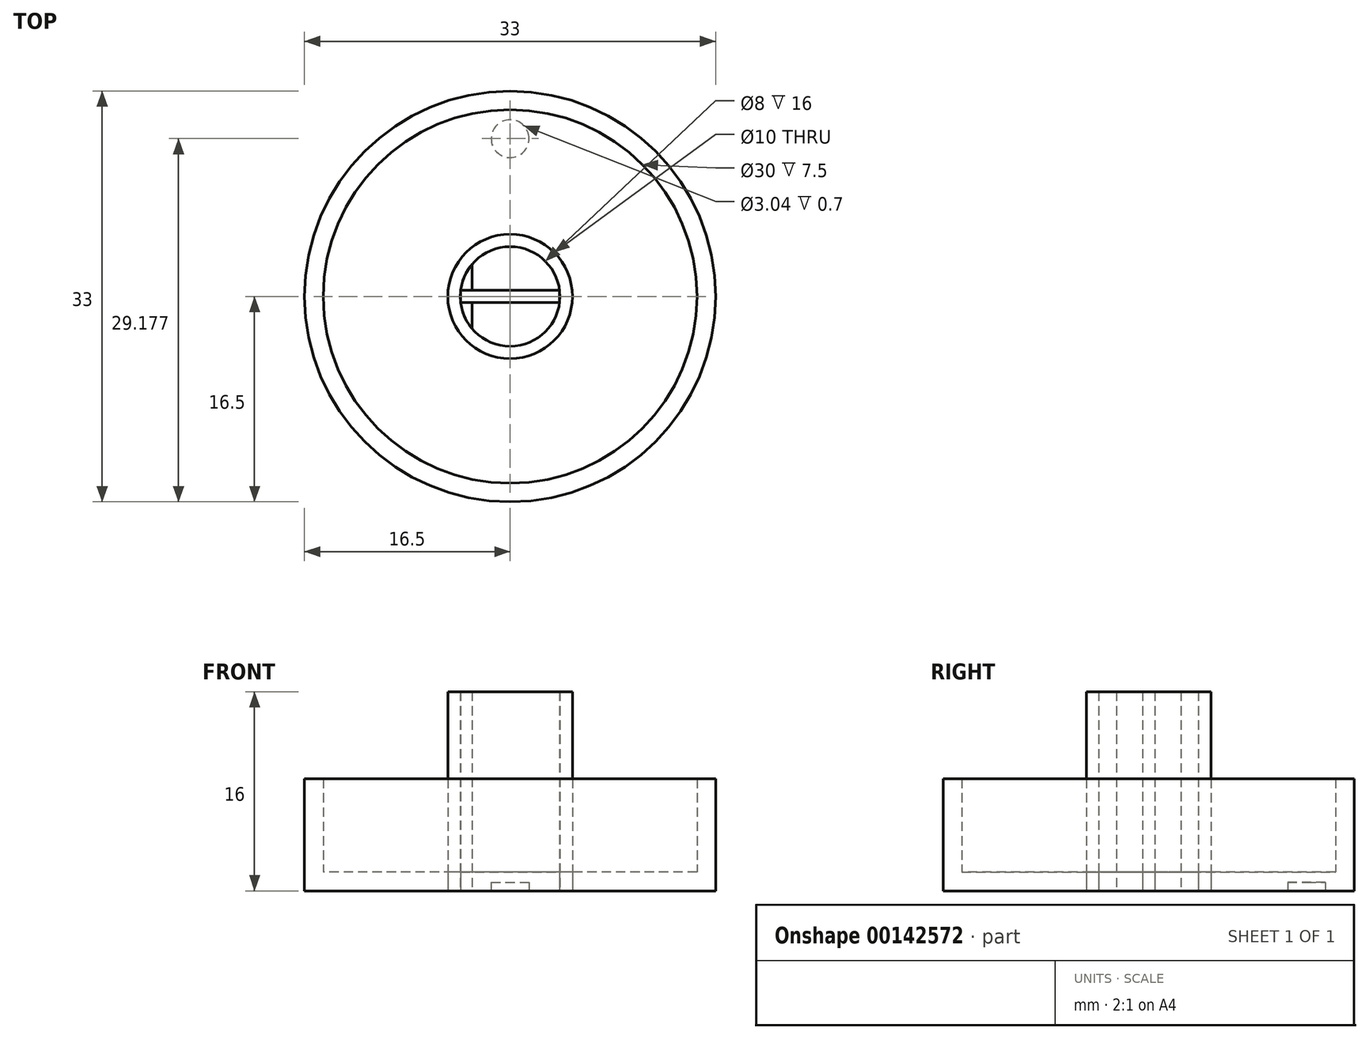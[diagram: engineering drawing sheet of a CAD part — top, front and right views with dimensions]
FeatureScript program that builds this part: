
annotation { "Feature Type Name" : "Feature", "Feature Type Description" : "" }
export const myFeature = defineFeature(function(context is Context, id is Id, definition is map)
    precondition{}
    {
        {
            var Q0;
            Q0=qCreatedBy(makeId("Top.planeOp"),FACE);
            var sketch = newSketch(context, id + "F0", { "sketchPlane" : qUnion([Q0])});
            skCircle(sketch, "E0", {"center": v(0, 0) * mm, "radius": 16.5 * mm});
            skCircle(sketch, "E1", {"center": v(0, 0) * mm, "radius": 15 * mm});
            skCircle(sketch, "E2", {"center": v(0, 0) * mm, "radius": 5 * mm});
            skCircle(sketch, "E3", {"center": v(0, 0) * mm, "radius": 4 * mm});
            skLineSegment(sketch, "E4.rect.bottom", {"start": v(-3.97, 0.5) * mm, "end": v(3.97, 0.5) * mm});
            skLineSegment(sketch, "E4.rect.top", {"start": v(-3.97, -0.5) * mm, "end": v(3.97, -0.5) * mm});
            skLineSegment(sketch, "E4.rect.left", {"start": v(-3.97, 0.5) * mm, "end": v(-3.97, -0.5) * mm});
            skLineSegment(sketch, "E4.rect.right", {"start": v(3.97, 0.5) * mm, "end": v(3.97, -0.5) * mm});
            skLineSegment(sketch, "E5", {"start": v(-3.05, 2.59) * mm, "end": v(-3.05, -2.59) * mm});
            skSolve(sketch);
        }
        {
            var Q0;
            Q0=makeQuery(id+"F0.imprint","IMPRINT",FACE,{"disambiguationData":[TD([[makeQuery(id+"F0.imprint","IMPRINT",EDGE,{"derivedFrom":sQuery(id+"F0.wireOp",EDGE,"E1")}),1.0]])]});
            var Q1;
            {var subQ0=sQuery(id+"F0.wireOp",EDGE,"E4.rect.bottom");Q1=makeQuery(id+"F0.imprint","IMPRINT",FACE,{"disambiguationData":[TD([[makeQuery(id+"F0.imprint","IMPRINT",EDGE,{"derivedFrom":subQ0}),1.0]])]});}
            var Q2;
            {var subQ0=sQuery(id+"F0.wireOp",EDGE,"E4.rect.top");Q2=makeQuery(id+"F0.imprint","IMPRINT",FACE,{"disambiguationData":[TD([[makeQuery(id+"F0.imprint","IMPRINT",EDGE,{"derivedFrom":subQ0}),-1.0]])]});}
            extrude(context, id + "F1", {"entities" : qUnion([Q0, Q1, Q2]), "depth" : 1.5 * mm});
        }
        {
            var Q0;
            Q0=qSketchRegion(id+"F0",true);
            extrude(context, id + "F2", {"entities" : qUnion([Q0]), "operationType" : NewBodyOperationType.ADD, "depth" : 9 * mm});
        }
        {
            var Q0;
            Q0=makeQuery(id+"F0.imprint","IMPRINT",FACE,{"disambiguationData":[TD([[makeQuery(id+"F0.imprint","IMPRINT",EDGE,{"derivedFrom":sQuery(id+"F0.wireOp",EDGE,"E2")}),1.0]])]});
            var Q1;
            Q1=makeQuery(id+"F0.imprint","IMPRINT",FACE,{"disambiguationData":[TD([[makeQuery(id+"F0.imprint","IMPRINT",EDGE,{"derivedFrom":sQuery(id+"F0.wireOp",EDGE,"E4.rect.bottom")}),-1.0]])]});
            extrude(context, id + "F3", {"entities" : qUnion([Q0, Q1]), "depth" : 16 * mm});
        }
        {
            var Q0;
            {var subQ1=sQuery(id+"F0.wireOp",EDGE,"E3");var subQ3=sQuery(id+"F0.wireOp",EDGE,"E5");var subQ4=makeQuery(id+"F0.imprint","INTERSECT",VERTEX,{"disambiguationData":[OD(0.0)],"derivedFrom":[subQ1,subQ3]});Q0=makeQuery(id+"F0.imprint","IMPRINT",FACE,{"disambiguationData":[TD([[makeQuery(id+"F0.imprint","IMPRINT",EDGE,{"disambiguationData":[TD([[subQ4,-1.0]])],"derivedFrom":subQ3}),-1.0]])]});}
            var Q1;
            {var subQ1=sQuery(id+"F0.wireOp",EDGE,"E3");var subQ3=sQuery(id+"F0.wireOp",EDGE,"E5");var subQ4=makeQuery(id+"F0.imprint","INTERSECT",VERTEX,{"disambiguationData":[OD(1.0)],"derivedFrom":[subQ1,subQ3]});Q1=makeQuery(id+"F0.imprint","IMPRINT",FACE,{"disambiguationData":[TD([[makeQuery(id+"F0.imprint","IMPRINT",EDGE,{"disambiguationData":[TD([[subQ4,1.0]])],"derivedFrom":subQ3}),-1.0]])]});}
            extrude(context, id + "F4", {"entities" : qUnion([Q0, Q1]), "depth" : 16 * mm});
        }
        {
            var Q0;
            {var subQ0=sQuery(id+"F0.wireOp",EDGE,"E1");Q0=makeQuery(id+"F2.boolean.opBoolean","MERGE",FACE,{"derivedFrom":[makeQuery(id+"F1.opExtrude","CAP_FACE",FACE,{"disambiguationData":[OSD([subQ0,sQuery(id+"F0.wireOp",EDGE,"E2")])],"isStart":true}),makeQuery(id+"F2.opExtrude","CAP_FACE",FACE,{"disambiguationData":[OSD([sQuery(id+"F0.wireOp",EDGE,"E0"),subQ0])],"isStart":true})]});}
            var sketch = newSketch(context, id + "F5", { "sketchPlane" : qUnion([Q0])});
            skCircle(sketch, "E6", {"center": v(0, -12.68) * mm, "radius": 1.52 * mm});
            skSolve(sketch);
        }
        {
            var Q0;
            Q0=makeQuery(id+"F5.imprint","IMPRINT",FACE,{"disambiguationData":[TD([[makeQuery(id+"F5.imprint","IMPRINT",EDGE,{"derivedFrom":sQuery(id+"F5.wireOp",EDGE,"E6")}),1.0]])]});
            extrude(context, id + "F6", {"entities" : qUnion([Q0]), "operationType" : NewBodyOperationType.REMOVE, "oppositeDirection" : true, "depth" : 0.7 * mm});
        }
    });
